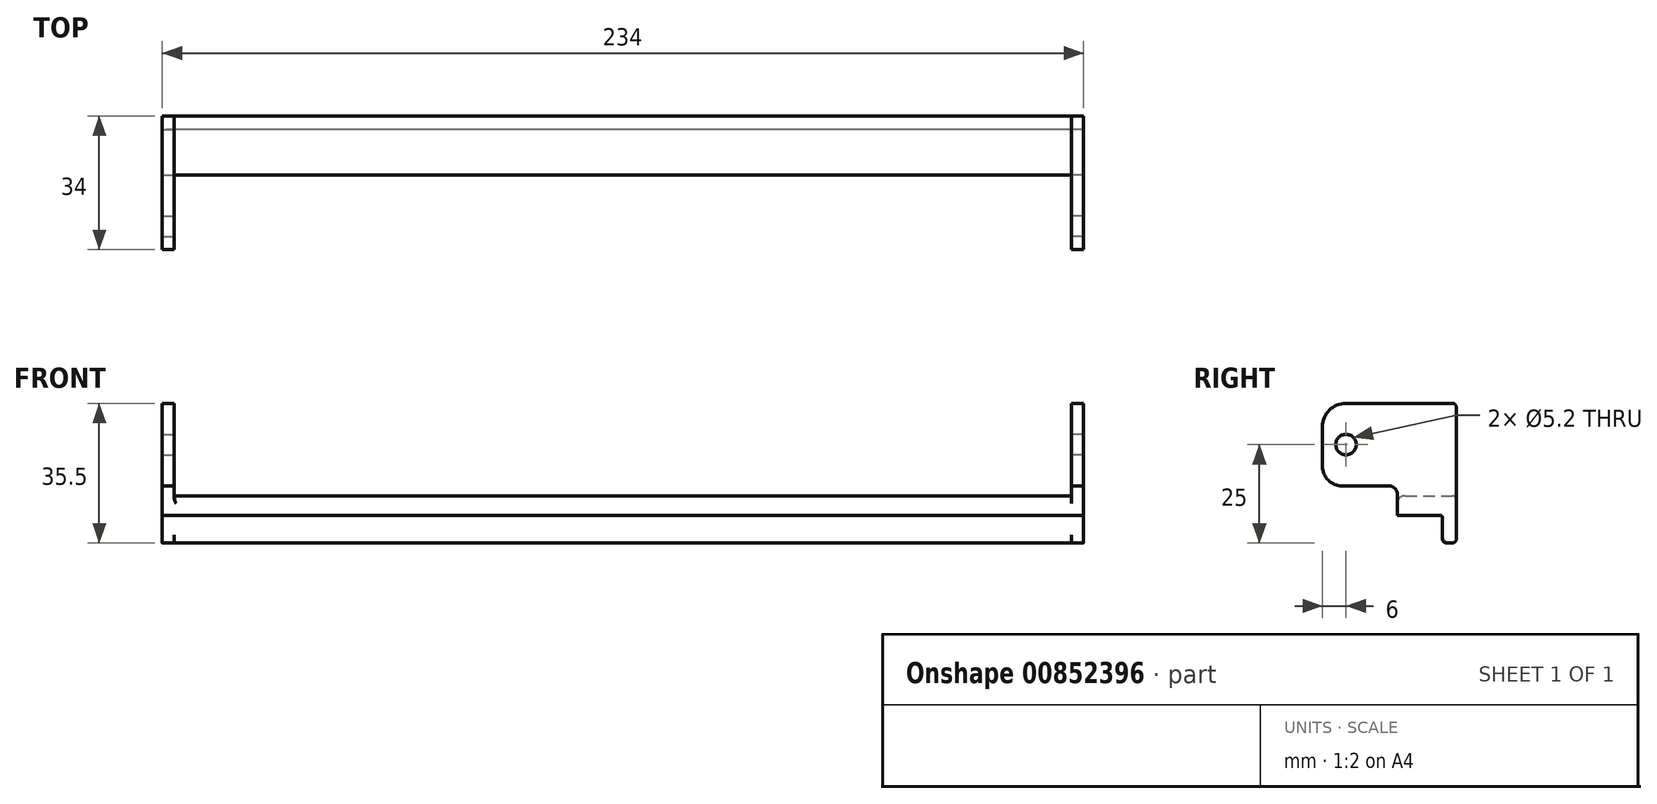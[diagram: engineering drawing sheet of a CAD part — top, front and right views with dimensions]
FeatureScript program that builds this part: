
annotation { "Feature Type Name" : "Feature", "Feature Type Description" : "" }
export const myFeature = defineFeature(function(context is Context, id is Id, definition is map)
    precondition{}
    {
        {
            var Q0;
            Q0=qCreatedBy(makeId("Right.planeOp"),FACE);
            var sketch = newSketch(context, id + "F0", { "sketchPlane" : qUnion([Q0])});
            skLineSegment(sketch, "E0.bottom", {"start": v(-9.5, 5) * mm, "end": v(2.5, 5) * mm});
            skLineSegment(sketch, "E0.top", {"start": v(-11.5, 0) * mm, "end": v(3.5, 0) * mm});
            skLineSegment(sketch, "E0.left", {"start": v(-11.5, 3) * mm, "end": v(-11.5, 0) * mm});
            skLineSegment(sketch, "E0.right", {"start": v(3.5, 4) * mm, "end": v(3.5, 0) * mm});
            skLineSegment(sketch, "E1.bottom", {"start": v(0, 0) * mm, "end": v(3.5, 0) * mm});
            skLineSegment(sketch, "E1.top", {"start": v(2, -7) * mm, "end": v(2.5, -7) * mm});
            skLineSegment(sketch, "E1.left", {"start": v(0, 0) * mm, "end": v(0, -5) * mm});
            skLineSegment(sketch, "E1.right", {"start": v(3.5, 0) * mm, "end": v(3.5, -6) * mm});
            skPoint(sketch, "E2.visualSharp", {"position": v(-11.5, 5) * mm});
            skArc(sketch, "E2.filletArc", {"start": v(-9.5, 5) * mm, "mid": v(-10.91, 4.41) * mm, "end": v(-11.5, 3) * mm});
            skPoint(sketch, "E3.visualSharp", {"position": v(0, -7) * mm});
            skArc(sketch, "E3.filletArc", {"start": v(0, -5) * mm, "mid": v(0.59, -6.41) * mm, "end": v(2, -7) * mm});
            skPoint(sketch, "E4.visualSharp", {"position": v(3.5, -7) * mm});
            skArc(sketch, "E4.filletArc", {"start": v(2.5, -7) * mm, "mid": v(3.2, -6.7) * mm, "end": v(3.5, -6) * mm});
            skPoint(sketch, "E5.visualSharp", {"position": v(3.5, 5) * mm});
            skArc(sketch, "E5.filletArc", {"start": v(3.5, 4) * mm, "mid": v(3.2, 4.7) * mm, "end": v(2.5, 5) * mm});
            skSolve(sketch);
        }
        {
            var Q0;
            Q0 = qSketchRegion(id + "F0", true);
            extrude(context, id + "F1", {"entities" : qUnion([Q0]), "endBound" : BoundingType.SYMMETRIC, "depth" : (150 + 78) * mm, "offsetDistance" : 25 * mm});
        }
        {
            var Q0;
            Q0=makeQuery(id+"F1.opExtrude","CAP_FACE",FACE,{"disambiguationData":[OSD([sQuery(id+"F0.wireOp",EDGE,"E0.bottom"),sQuery(id+"F0.wireOp",EDGE,"E0.top"),sQuery(id+"F0.wireOp",EDGE,"E0.left"),sQuery(id+"F0.wireOp",EDGE,"E0.right"),sQuery(id+"F0.wireOp",EDGE,"E1.top"),sQuery(id+"F0.wireOp",EDGE,"E1.left"),sQuery(id+"F0.wireOp",EDGE,"E1.right")])],"isStart":false});
            var sketch = newSketch(context, id + "F2", { "sketchPlane" : qUnion([Q0])});
            skLineSegment(sketch, "E6.bottom", {"start": v(-24.5, 28.5) * mm, "end": v(2.5, 28.5) * mm});
            skLineSegment(sketch, "E6.top", {"start": v(-25.5, 7.5) * mm, "end": v(-13.5, 7.5) * mm});
            skLineSegment(sketch, "E6.left", {"start": v(-30.5, 22.5) * mm, "end": v(-30.5, 12.5) * mm});
            skLineSegment(sketch, "E6.right", {"start": v(3.5, 27.5) * mm, "end": v(3.5, 7.5) * mm});
            skLineSegment(sketch, "E7.0", {"start": v(3.5, 7.5) * mm, "end": v(3.5, -6) * mm});
            skLineSegment(sketch, "E8.0", {"start": v(-11.5, 5.5) * mm, "end": v(-11.5, 0) * mm});
            skLineSegment(sketch, "E9.0", {"start": v(-11.5, 0) * mm, "end": v(0, 0) * mm});
            skLineSegment(sketch, "E10.0", {"start": v(0, 0) * mm, "end": v(0, -6) * mm});
            skLineSegment(sketch, "E11.0", {"start": v(1, -7) * mm, "end": v(2.5, -7) * mm});
            skPoint(sketch, "E12.orphan", {"position": v(-11.5, 3) * mm});
            skPoint(sketch, "E13.orphan", {"position": v(3.5, 4) * mm});
            skLineSegment(sketch, "E14.trimOffspring", {"start": v(3.5, 7.5) * mm, "end": v(3.5, 7.5) * mm});
            skPoint(sketch, "E15.visualSharp", {"position": v(3.5, 28.5) * mm});
            skArc(sketch, "E15.filletArc", {"start": v(3.5, 27.5) * mm, "mid": v(3.2, 28.2) * mm, "end": v(2.5, 28.5) * mm});
            skPoint(sketch, "E16.visualSharp", {"position": v(-30.5, 28.5) * mm});
            skArc(sketch, "E16.filletArc", {"start": v(-24.5, 28.5) * mm, "mid": v(-28.74, 26.74) * mm, "end": v(-30.5, 22.5) * mm});
            skPoint(sketch, "E17.visualSharp", {"position": v(-30.5, 7.5) * mm});
            skArc(sketch, "E17.filletArc", {"start": v(-30.5, 12.5) * mm, "mid": v(-29.04, 8.96) * mm, "end": v(-25.5, 7.5) * mm});
            skPoint(sketch, "E18.visualSharp", {"position": v(-11.5, 7.5) * mm});
            skArc(sketch, "E18.filletArc", {"start": v(-11.5, 5.5) * mm, "mid": v(-12.09, 6.91) * mm, "end": v(-13.5, 7.5) * mm});
            skPoint(sketch, "E19.newPointA", {"position": v(0, -5) * mm});
            skArc(sketch, "E19.filletArc", {"start": v(0, -6) * mm, "mid": v(0.3, -6.7) * mm, "end": v(1, -7) * mm});
            skPoint(sketch, "E20.newPointB", {"position": v(3.5, -6) * mm});
            skArc(sketch, "E20.filletArc", {"start": v(2.5, -7) * mm, "mid": v(3.2, -6.7) * mm, "end": v(3.5, -6) * mm});
            skPoint(sketch, "E21", {"position": v(-24.5, 18) * mm});
            skSolve(sketch);
        }
        {
            var Q0;
            Q0 = qSketchRegion(id + "F2", true);
            extrude(context, id + "F3", {"entities" : qUnion([Q0]), "depth" : 3 * mm, "offsetDistance" : 25 * mm});
        }
        {
            var Q0;
            Q0=makeQuery(id+"F3.opExtrude","SWEPT_BODY",BODY,{"disambiguationData":[OSD([sQuery(id+"F2.wireOp",EDGE,"E6.bottom"),sQuery(id+"F2.wireOp",EDGE,"E6.top"),sQuery(id+"F2.wireOp",EDGE,"E6.left"),sQuery(id+"F2.wireOp",EDGE,"E6.right"),sQuery(id+"F2.wireOp",EDGE,"E7.0"),sQuery(id+"F2.wireOp",EDGE,"E8.0"),sQuery(id+"F2.wireOp",EDGE,"E9.0"),sQuery(id+"F2.wireOp",EDGE,"E10.0"),sQuery(id+"F2.wireOp",EDGE,"E11.0")])]});
            var Q1;
            Q1=qCreatedBy(makeId("Right.planeOp"),FACE);
            mirror(context, id + "F4", {"operationType" : NewBodyOperationType.ADD, "entities" : qUnion([Q0]), "mirrorPlane" : qUnion([Q1])});
        }
        {
            var Q0;
            {var subQ0=makeQuery(id+"F3.opExtrude","SWEPT_EDGE",EDGE,{"disambiguationData":[OSD([sQuery(id+"F2.wireOp",EDGE,"E9.0"),sQuery(id+"F2.wireOp",EDGE,"E10.0")])]});Q0=makeQuery(id+"F4.boolean.opBoolean","MERGE",EDGE,{"derivedFrom":[makeQuery(id+"F1.opExtrude","SWEPT_EDGE",EDGE,{"disambiguationData":[OSD([sQuery(id+"F0.wireOp",EDGE,"E0.top"),sQuery(id+"F0.wireOp",EDGE,"E1.bottom"),sQuery(id+"F0.wireOp",EDGE,"E1.left")])]}),subQ0,makeQuery(id+"F4.opPattern","COPY",EDGE,{"derivedFrom":subQ0,"instanceName":"1"})]});}
            fillet(context, id + "F5", {"entities" : qUnion([Q0]), "radius" : .5 * mm, "tangentPropagation" : true, "allowEdgeOverflow" : false});
        }
        {
            var Q0;
            Q0=sQuery(id+"F2.wireOp",VERTEX,"E21");
            var Q1;
            Q1=makeQuery(id+"F1.opExtrude","SWEPT_BODY",BODY,{"disambiguationData":[OSD([sQuery(id+"F0.wireOp",EDGE,"E0.bottom"),sQuery(id+"F0.wireOp",EDGE,"E0.top"),sQuery(id+"F0.wireOp",EDGE,"E0.left"),sQuery(id+"F0.wireOp",EDGE,"E0.right"),sQuery(id+"F0.wireOp",EDGE,"E1.top"),sQuery(id+"F0.wireOp",EDGE,"E1.left"),sQuery(id+"F0.wireOp",EDGE,"E1.right"),sQuery(id+"F0.wireOp",EDGE,"E2.filletArc"),sQuery(id+"F0.wireOp",EDGE,"E3.filletArc"),sQuery(id+"F0.wireOp",EDGE,"E4.filletArc"),sQuery(id+"F0.wireOp",EDGE,"E5.filletArc")])]});
            hole(context, id + "F6", {"style" : HoleStyle.SIMPLE, "endStyle" : HoleEndStyle.THROUGH, "holeDiameter" : 5.2 * mm, "majorDiameter" : 5 * mm, "isTappedThrough" : true, "tappedDepth" : 12 * mm, "tapClearance" : 3, "startFromSketch" : true, "locations" : qUnion([Q0]), "scope" : qUnion([Q1])});
        }
        {
            var Q0;
            Q0=sQuery(id+"F2.wireOp",VERTEX,"E21");
            var Q1;
            Q1=makeQuery(id+"F1.opExtrude","SWEPT_BODY",BODY,{"disambiguationData":[OSD([sQuery(id+"F0.wireOp",EDGE,"E0.bottom"),sQuery(id+"F0.wireOp",EDGE,"E0.top"),sQuery(id+"F0.wireOp",EDGE,"E0.left"),sQuery(id+"F0.wireOp",EDGE,"E0.right"),sQuery(id+"F0.wireOp",EDGE,"E1.top"),sQuery(id+"F0.wireOp",EDGE,"E1.left"),sQuery(id+"F0.wireOp",EDGE,"E1.right"),sQuery(id+"F0.wireOp",EDGE,"E2.filletArc"),sQuery(id+"F0.wireOp",EDGE,"E3.filletArc"),sQuery(id+"F0.wireOp",EDGE,"E4.filletArc"),sQuery(id+"F0.wireOp",EDGE,"E5.filletArc")])]});
            hole(context, id + "F7", {"style" : HoleStyle.SIMPLE, "endStyle" : HoleEndStyle.THROUGH, "oppositeDirection" : true, "holeDiameter" : 5.2 * mm, "majorDiameter" : 5 * mm, "isTappedThrough" : true, "tappedDepth" : 12 * mm, "tapClearance" : 3, "startFromSketch" : true, "locations" : qUnion([Q0]), "scope" : qUnion([Q1])});
        }
        {
            var Q0;
            Q0=makeQuery(id+"F1.opExtrude","CAP_EDGE",EDGE,{"disambiguationData":[OSD([sQuery(id+"F0.wireOp",EDGE,"E0.bottom")])],"isStart":true});
            var Q1;
            Q1=makeQuery(id+"F1.opExtrude","CAP_EDGE",EDGE,{"disambiguationData":[OSD([sQuery(id+"F0.wireOp",EDGE,"E0.bottom")])],"isStart":false});
            fillet(context, id + "F8", {"entities" : qUnion([Q0, Q1]), "radius" : .5 * mm, "tangentPropagation" : true, "allowEdgeOverflow" : false});
        }
    });
